# Revit family: Storage-Mounted-Teknion-B_HCL_Standard_Hutch_Solid_Hinged_Doors-R2019
name_source: partatom
category: Furniture
units: mm (PartAtom-declared; Revit-internal decimal feet)

## family parameters
Always vertical = Yes
Cut with Voids When Loaded = No
OmniClass Number = 23.40.20.00
OmniClass Title = General Furniture and Specialties
Room Calculation Point = No
Shared = Yes
Work Plane-Based = No

## types (6) — shared parameters
Assembly Code = E2020200
Manufacturer = Teknion
Manufacturer Fax = 416.661.4586
Part Number = B_HCL
Product Documentation Link = https://www.teknion.com
Product Line = Expansion Casegoods
Product Page URL = https://www.teknion.com
Series = Expansion Casegoods
Sustainability Data = https://www.teknion.com
URL = www.teknion.com
Unit Weight URL = http://www.teknion.com
Warranty = http://www.teknion.com

## per-type parameters (varying)
| type | Bottom Height Offset | Description | Height | Model |
| 1" Worksurface Thickness, 37" Height | 28.823 " | Standard Hutch - Solid Hinged Doors, 1" Worksurface Thickness, 15" Depth, 37" Height | 36.354 " | BDHCL15__37 |
| 1" Worksurface Thickness, 43" Height | 28.823 " | Standard Hutch - Solid Hinged Doors, 1" Worksurface Thickness, 15" Depth, 43" Height | 42.594 " | BDHCL15__43 |
| 1-3/16" Worksurface Thickness, 37" Height | 28.996 " | Standard Hutch - Solid Hinged Doors, 1-3/16" Worksurface Thickness, 15" Depth, 37" Height | 36.354 " | BMHCL15__37 |
| 1-3/16" Worksurface Thickness, 43" Height | 28.996 " | Standard Hutch - Solid Hinged Doors, 1-3/16" Worksurface Thickness, 15" Depth, 43" Height | 42.594 " | BMHCL15__43 |
| 1-9/16" Worksurface Thickness, 43" Height | 29.362 " | Standard Hutch - Solid Hinged Doors, 1-9/16" Worksurface Thickness, 15" Depth, 43" Height | 42.594 " | BXHCL15__43 |
| 1-9/16" Worksurface Thickness, 37" Height | 29.362 " | Standard Hutch - Solid Hinged Doors, 1-9/16" Worksurface Thickness, 15" Depth, 37" Height | 36.354 " | BXHCL15__37 |

## geometry (parser evidence)
native form markers: Sweep x2
no freeform markers — native parametric forms only
